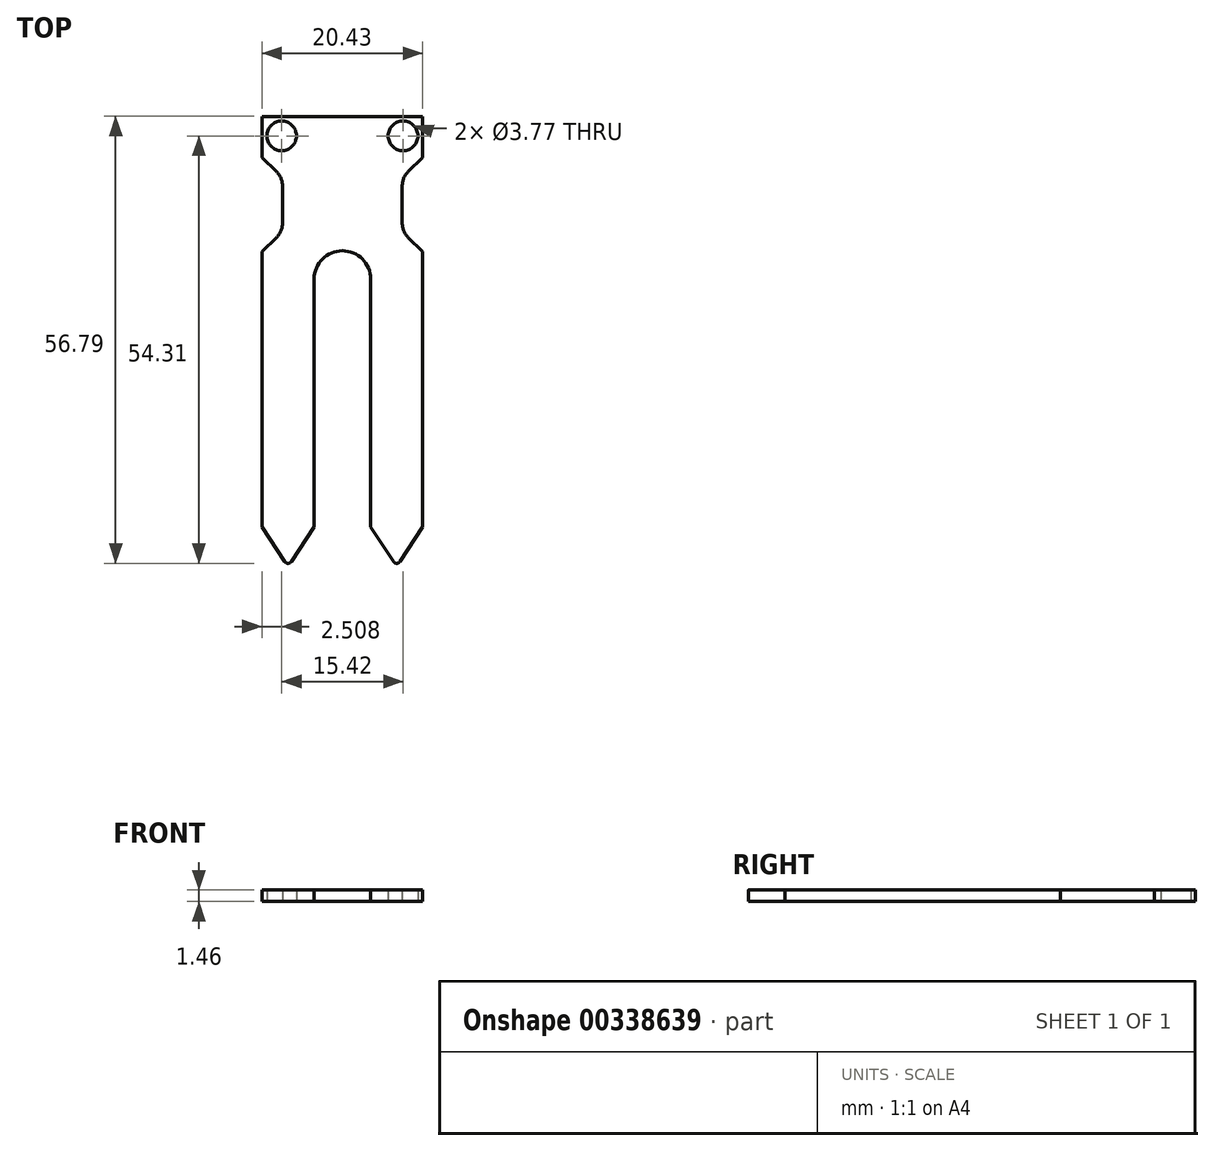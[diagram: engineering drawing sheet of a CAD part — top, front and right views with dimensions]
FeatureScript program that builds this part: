
annotation { "Feature Type Name" : "Feature", "Feature Type Description" : "" }
export const myFeature = defineFeature(function(context is Context, id is Id, definition is map)
    precondition{}
    {
        {
            var Q0;
            Q0=qCreatedBy(makeId("Top.planeOp"),FACE);
            var sketch = newSketch(context, id + "F0", { "sketchPlane" : qUnion([Q0])});
            skPoint(sketch, "E0.middle", {"position": v(0, 10.38) * mm});
            skLineSegment(sketch, "E1.bottom", {"start": v(-10.2, 20.7) * mm, "end": v(10.22, 20.7) * mm});
            skLineSegment(sketch, "E1.top", {"start": v(-10.2, 0.05) * mm, "end": v(10.22, 0.05) * mm, "construction": true});
            skLineSegment(sketch, "E1.left", {"start": v(-10.2, 20.7) * mm, "end": v(-10.2, 0.05) * mm});
            skLineSegment(sketch, "E1.right", {"start": v(10.22, 20.7) * mm, "end": v(10.22, 0.05) * mm});
            skArc(sketch, "E2", {"start": v(3.6, 0.05) * mm, "mid": v(0, 3.63) * mm, "end": v(-3.58, 0.05) * mm});
            skLineSegment(sketch, "E3", {"start": v(10.22, 20.7) * mm, "end": v(10.22, 15.48) * mm, "construction": true});
            skLineSegment(sketch, "E4", {"start": v(10.22, 15.48) * mm, "end": v(10.22, 3.54) * mm, "construction": true});
            skLineSegment(sketch, "E5", {"start": v(0, 10.38) * mm, "end": v(0, -15.23) * mm, "construction": true});
            skPoint(sketch, "E5.endSnap0", {"position": v(0, 3.63) * mm});
            skCircle(sketch, "E6", {"center": v(7.72, 18.23) * mm, "radius": 1.89 * mm});
            skCircle(sketch, "E7.MirrorC", {"center": v(-7.7, 18.23) * mm, "radius": 1.89 * mm});
            skLineSegment(sketch, "E8", {"start": v(6.9, -36.48) * mm, "end": v(6.9, 0.05) * mm, "construction": true});
            skPoint(sketch, "E9.oppositeSnap0", {"position": v(7.65, -15.51) * mm});
            skLineSegment(sketch, "E10", {"start": v(10.22, 0.05) * mm, "end": v(10.22, -31.46) * mm});
            skLineSegment(sketch, "E11", {"start": v(10.22, -31.46) * mm, "end": v(6.9, -36.48) * mm});
            skLineSegment(sketch, "E12.MirrorCS", {"start": v(3.6, -31.46) * mm, "end": v(6.9, -36.48) * mm});
            skLineSegment(sketch, "E13.MirrorCS", {"start": v(3.6, 0.05) * mm, "end": v(3.6, -31.46) * mm});
            skLineSegment(sketch, "E14.MirrorCS", {"start": v(-3.58, 0.05) * mm, "end": v(-3.58, -31.46) * mm});
            skLineSegment(sketch, "E15.MirrorCS", {"start": v(-3.58, -31.46) * mm, "end": v(-6.9, -36.48) * mm});
            skLineSegment(sketch, "E16.MirrorCS", {"start": v(-10.2, -31.46) * mm, "end": v(-6.9, -36.48) * mm});
            skLineSegment(sketch, "E17.MirrorCS", {"start": v(-10.2, 0.05) * mm, "end": v(-10.2, -31.46) * mm});
            skLineSegment(sketch, "E18", {"start": v(10.22, 3.54) * mm, "end": v(10.22, 6.08) * mm, "construction": true});
            skLineSegment(sketch, "E19", {"start": v(10.22, 9.5) * mm, "end": v(6.5, 9.5) * mm, "construction": true});
            skLineSegment(sketch, "E20.MirrorCS", {"start": v(10.22, 15.48) * mm, "end": v(10.22, 12.94) * mm, "construction": true});
            skPoint(sketch, "E21.endSnap0", {"position": v(8.36, 9.5) * mm});
            skLineSegment(sketch, "E22", {"start": v(10.22, 12.94) * mm, "end": v(7.61, 12.94) * mm, "construction": true});
            skLineSegment(sketch, "E23", {"start": v(10.22, 15.48) * mm, "end": v(7.61, 12.94) * mm});
            skLineSegment(sketch, "E24.MirrorCS", {"start": v(10.22, 3.54) * mm, "end": v(7.61, 6.08) * mm});
            skLineSegment(sketch, "E25", {"start": v(7.61, 12.94) * mm, "end": v(7.61, 6.08) * mm});
            skLineSegment(sketch, "E26.MirrorCS", {"start": v(-10.2, 15.48) * mm, "end": v(-7.6, 12.94) * mm});
            skLineSegment(sketch, "E27.MirrorCS", {"start": v(-7.6, 12.94) * mm, "end": v(-7.6, 6.08) * mm});
            skLineSegment(sketch, "E28.MirrorCS", {"start": v(-10.2, 3.54) * mm, "end": v(-7.6, 6.08) * mm});
            skSolve(sketch);
        }
        {
            var Q0;
            Q0=makeQuery(id+"F0.imprint","IMPRINT",FACE,{"disambiguationData":[TD([[makeQuery(id+"F0.imprint","IMPRINT",EDGE,{"derivedFrom":sQuery(id+"F0.wireOp",EDGE,"E9.bottom")}),-1.0]])]});
            var Q1;
            {var subQ3=sQuery(id+"F0.wireOp",EDGE,"E1.bottom");Q1=makeQuery(id+"F0.imprint","IMPRINT",FACE,{"disambiguationData":[TD([[makeQuery(id+"F0.imprint","IMPRINT",EDGE,{"derivedFrom":subQ3}),-1.0]])]});}
            extrude(context, id + "F1", {"entities" : qUnion([Q0, Q1]), "depth" : 1.46 * mm});
        }
        {
            var Q0;
            Q0=makeQuery(id+"F1.opExtrude","SWEPT_EDGE",EDGE,{"disambiguationData":[OSD([sQuery(id+"F0.wireOp",EDGE,"E23"),sQuery(id+"F0.wireOp",EDGE,"E25")])]});
            fillet(context, id + "F2", {"entities" : qUnion([Q0]), "radius" : 2.5 * mm, "tangentPropagation" : true, "allowEdgeOverflow" : false});
        }
        {
            var Q0;
            Q0=makeQuery(id+"F1.opExtrude","SWEPT_EDGE",EDGE,{"disambiguationData":[OSD([sQuery(id+"F0.wireOp",EDGE,"E26.MirrorCS"),sQuery(id+"F0.wireOp",EDGE,"E27.MirrorCS")])]});
            var Q1;
            Q1=makeQuery(id+"F1.opExtrude","SWEPT_EDGE",EDGE,{"disambiguationData":[OSD([sQuery(id+"F0.wireOp",EDGE,"E27.MirrorCS"),sQuery(id+"F0.wireOp",EDGE,"E28.MirrorCS")])]});
            var Q2;
            Q2=makeQuery(id+"F1.opExtrude","SWEPT_EDGE",EDGE,{"disambiguationData":[OSD([sQuery(id+"F0.wireOp",EDGE,"E24.MirrorCS"),sQuery(id+"F0.wireOp",EDGE,"E25")])]});
            fillet(context, id + "F3", {"entities" : qUnion([Q0, Q1, Q2]), "radius" : 2.5 * mm, "tangentPropagation" : true, "allowEdgeOverflow" : false});
        }
        {
            var Q0;
            Q0=makeQuery(id+"F1.opExtrude","SWEPT_EDGE",EDGE,{"disambiguationData":[OSD([sQuery(id+"F0.wireOp",EDGE,"E11"),sQuery(id+"F0.wireOp",EDGE,"E12.MirrorCS")])]});
            var Q1;
            Q1=makeQuery(id+"F1.opExtrude","SWEPT_EDGE",EDGE,{"disambiguationData":[OSD([sQuery(id+"F0.wireOp",EDGE,"E15.MirrorCS"),sQuery(id+"F0.wireOp",EDGE,"E16.MirrorCS")])]});
            fillet(context, id + "F4", {"entities" : qUnion([Q0, Q1]), "radius" : 0.5 * mm, "tangentPropagation" : true, "allowEdgeOverflow" : false});
        }
    });
